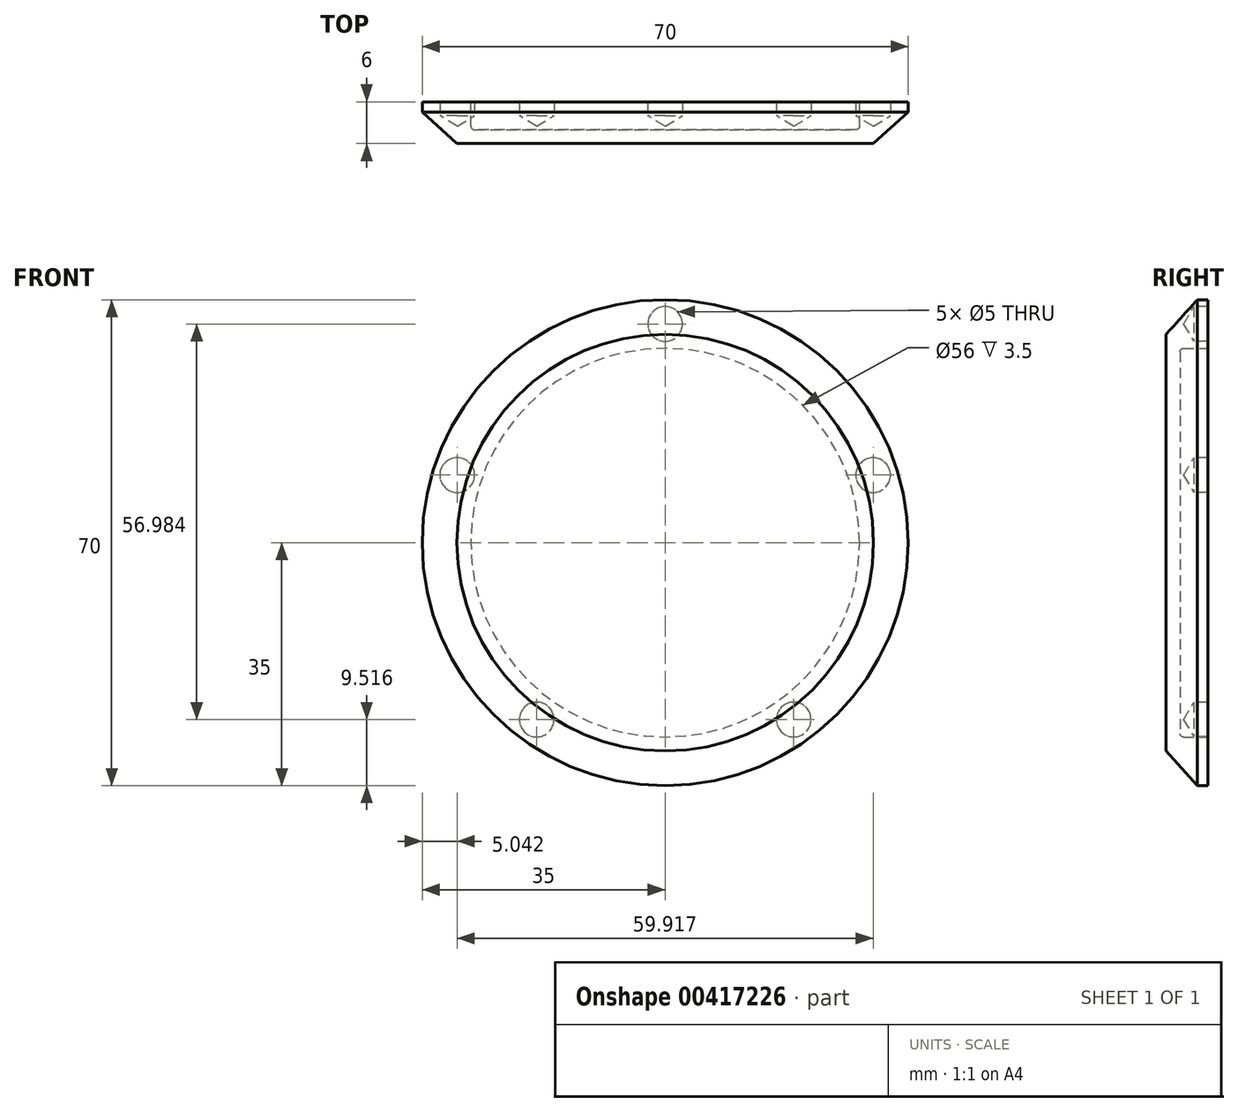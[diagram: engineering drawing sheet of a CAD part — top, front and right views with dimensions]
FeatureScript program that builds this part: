
annotation { "Feature Type Name" : "Feature", "Feature Type Description" : "" }
export const myFeature = defineFeature(function(context is Context, id is Id, definition is map)
    precondition{}
    {
        {
            var Q0;
            Q0=qCreatedBy(makeId("Top.planeOp"),FACE);
            var sketch = newSketch(context, id + "F0", { "sketchPlane" : qUnion([Q0])});
            skLineSegment(sketch, "E0", {"start": v(-35, 0) * mm, "end": v(-35, -1.5) * mm});
            skLineSegment(sketch, "E1", {"start": v(-35, -1.5) * mm, "end": v(-30, -6) * mm});
            skLineSegment(sketch, "E2", {"start": v(-28, -3.5) * mm, "end": v(-28, 0) * mm});
            skLineSegment(sketch, "E3", {"start": v(-28, 0) * mm, "end": v(-35, 0) * mm});
            skLineSegment(sketch, "E4", {"start": v(-27.5, -4) * mm, "end": v(0, -4) * mm});
            skLineSegment(sketch, "E5", {"start": v(0, -4) * mm, "end": v(0, -6) * mm});
            skLineSegment(sketch, "E6", {"start": v(0, -6) * mm, "end": v(-30, -6) * mm});
            skPoint(sketch, "E7.visualSharp", {"position": v(-28, -4) * mm});
            skArc(sketch, "E7.filletArc", {"start": v(-28, -3.5) * mm, "mid": v(-27.85, -3.85) * mm, "end": v(-27.5, -4) * mm});
            skLineSegment(sketch, "E8", {"start": v(0, 19.96) * mm, "end": v(0, -24.45) * mm, "construction": true});
            skSolve(sketch);
        }
        {
            var Q0;
            Q0=makeQuery(id+"F0.imprint","IMPRINT",FACE,{"disambiguationData":[TD([[makeQuery(id+"F0.imprint","IMPRINT",EDGE,{"derivedFrom":sQuery(id+"F0.wireOp",EDGE,"E0")}),1.0]])]});
            var Q1;
            Q1=sQuery(id+"F0.wireOp",EDGE,"E8");
            revolve(context, id + "F1", {"entities" : qUnion([Q0]), "axis" : qUnion([Q1]), "revolveType" : RevolveType.FULL});
        }
        {
            var Q0;
            Q0=qCreatedBy(makeId("Front.planeOp"),FACE);
            var sketch = newSketch(context, id + "F2", { "sketchPlane" : qUnion([Q0])});
            skCircle(sketch, "E9", {"center": v(0, 0) * mm, "radius": 31.5 * mm, "construction": true});
            skPoint(sketch, "E10", {"position": v(0, 31.5) * mm});
            skPoint(sketch, "E11.1.0", {"position": v(-29.96, 9.73) * mm});
            skPoint(sketch, "E11.2.0", {"position": v(-18.52, -25.48) * mm});
            skPoint(sketch, "E11.3.0", {"position": v(18.52, -25.48) * mm});
            skPoint(sketch, "E11.4.0", {"position": v(29.96, 9.73) * mm});
            skSolve(sketch);
        }
        {
            var Q0;
            Q0=sQuery(id+"F2.wireOp",VERTEX,"E10");
            var Q1;
            Q1=sQuery(id+"F2.wireOp",VERTEX,"E11.4.0");
            var Q2;
            Q2=sQuery(id+"F2.wireOp",VERTEX,"E11.3.0");
            var Q3;
            Q3=sQuery(id+"F2.wireOp",VERTEX,"E11.2.0");
            var Q4;
            Q4=sQuery(id+"F2.wireOp",VERTEX,"E11.1.0");
            var Q5;
            Q5=makeQuery(id+"F1.opRevolve","SWEPT_BODY",BODY,{"disambiguationData":[OSD([sQuery(id+"F0.wireOp",EDGE,"E0"),sQuery(id+"F0.wireOp",EDGE,"E1"),sQuery(id+"F0.wireOp",EDGE,"E2"),sQuery(id+"F0.wireOp",EDGE,"E3"),sQuery(id+"F0.wireOp",EDGE,"E4"),sQuery(id+"F0.wireOp",EDGE,"E5"),sQuery(id+"F0.wireOp",EDGE,"E6"),sQuery(id+"F0.wireOp",EDGE,"E7.filletArc")])]});
            hole(context, id + "F3", {"style" : HoleStyle.SIMPLE, "endStyle" : HoleEndStyle.BLIND, "oppositeDirection" : true, "holeDiameter" : 5 * mm, "holeDepth" : 2 * mm, "isTappedThrough" : true, "tappedDepth" : 12 * mm, "tapClearance" : 3, "locations" : qUnion([Q0, Q1, Q2, Q3, Q4]), "scope" : qUnion([Q5]), "startStyle" : HoleStartStyle.PART});
        }
    });
